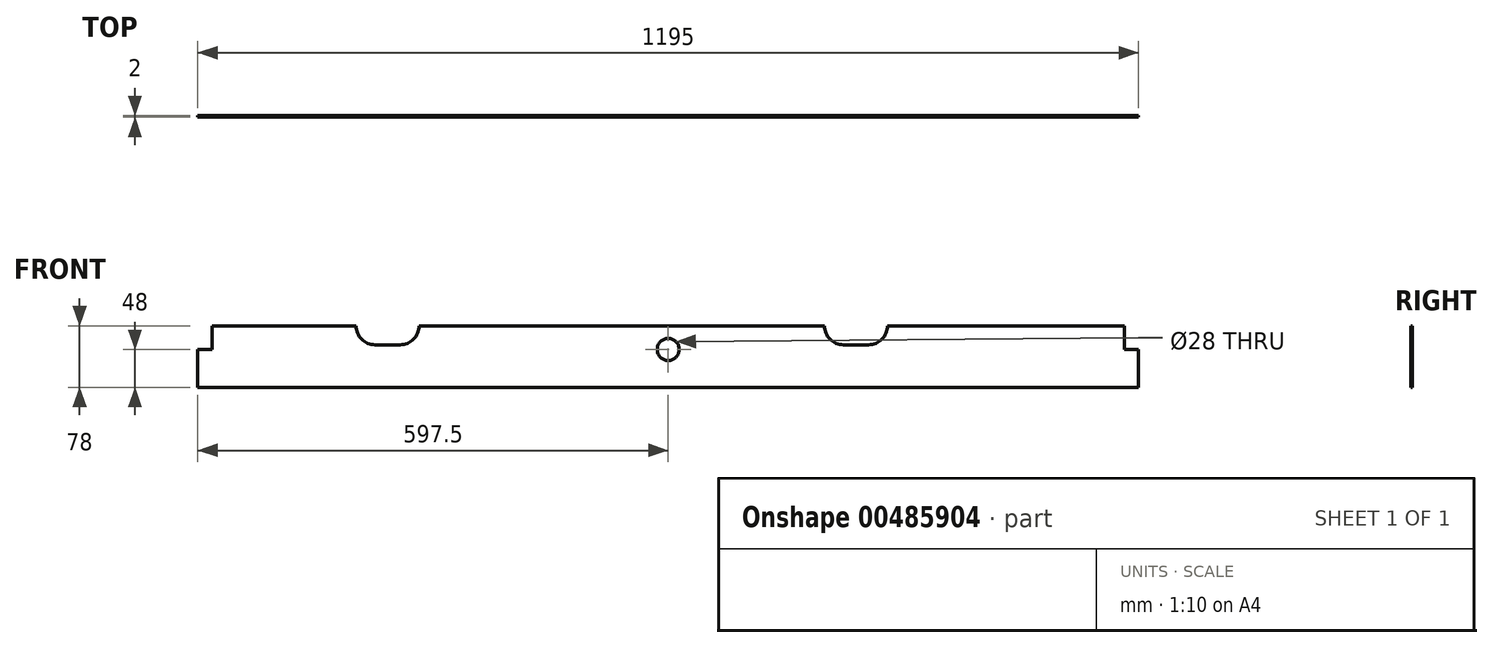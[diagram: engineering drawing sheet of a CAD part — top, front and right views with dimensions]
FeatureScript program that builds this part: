
annotation { "Feature Type Name" : "Feature", "Feature Type Description" : "" }
export const myFeature = defineFeature(function(context is Context, id is Id, definition is map)
    precondition{}
    {
        {
            var Q0;
            Q0=qCreatedBy(makeId("Front.planeOp"),FACE);
            var sketch = newSketch(context, id + "F0", { "sketchPlane" : qUnion([Q0])});
            skLineSegment(sketch, "E0.bottom", {"start": v(597.5, -39) * mm, "end": v(-597.5, -39) * mm});
            skLineSegment(sketch, "E0.top", {"start": v(579.5, 39) * mm, "end": v(278.5, 39) * mm});
            skLineSegment(sketch, "E0.left", {"start": v(597.5, -39) * mm, "end": v(597.5, 9) * mm});
            skLineSegment(sketch, "E0.right", {"start": v(-597.5, -39) * mm, "end": v(-597.5, 9) * mm});
            skPoint(sketch, "E0.middle", {"position": v(0, 0) * mm});
            skLineSegment(sketch, "E1.top", {"start": v(-597.5, 9) * mm, "end": v(-579.5, 9) * mm});
            skLineSegment(sketch, "E1.right", {"start": v(-579.5, 39) * mm, "end": v(-579.5, 9) * mm});
            skPoint(sketch, "E2.orphan", {"position": v(-597.5, 39) * mm});
            skLineSegment(sketch, "E3.top", {"start": v(597.5, 9) * mm, "end": v(579.5, 9) * mm});
            skLineSegment(sketch, "E3.right", {"start": v(579.5, 39) * mm, "end": v(579.5, 9) * mm});
            skPoint(sketch, "E4.orphan", {"position": v(597.5, 39) * mm});
            skLineSegment(sketch, "E5.top", {"start": v(-372.5, 15) * mm, "end": v(-340.5, 15) * mm});
            skLineSegment(sketch, "E5.left", {"start": v(-396.5, 39) * mm, "end": v(-396.5, 39) * mm});
            skPoint(sketch, "E6.visualSharp", {"position": v(-396.5, 15) * mm});
            skArc(sketch, "E6.filletArc", {"start": v(-396.5, 39) * mm, "mid": v(-389.47, 22.03) * mm, "end": v(-372.5, 15) * mm});
            skPoint(sketch, "E7.visualSharp", {"position": v(-316.5, 15) * mm});
            skArc(sketch, "E7.filletArc", {"start": v(-340.5, 15) * mm, "mid": v(-323.53, 22.03) * mm, "end": v(-316.5, 39) * mm});
            skLineSegment(sketch, "E8.trimOffspring", {"start": v(-396.5, 39) * mm, "end": v(-579.5, 39) * mm});
            skLineSegment(sketch, "E9.top", {"start": v(254.5, 15) * mm, "end": v(222.5, 15) * mm});
            skLineSegment(sketch, "E9.left", {"start": v(278.5, 39) * mm, "end": v(278.5, 39) * mm});
            skPoint(sketch, "E10.visualSharp", {"position": v(198.5, 15) * mm});
            skArc(sketch, "E10.filletArc", {"start": v(198.5, 39) * mm, "mid": v(205.53, 22.03) * mm, "end": v(222.5, 15) * mm});
            skPoint(sketch, "E11.visualSharp", {"position": v(278.5, 15) * mm});
            skArc(sketch, "E11.filletArc", {"start": v(254.5, 15) * mm, "mid": v(271.47, 22.03) * mm, "end": v(278.5, 39) * mm});
            skLineSegment(sketch, "E12.trimOffspring", {"start": v(198.5, 39) * mm, "end": v(-316.5, 39) * mm});
            skCircle(sketch, "E13", {"center": v(0, 9) * mm, "radius": 14 * mm});
            skSolve(sketch);
        }
        {
            var Q0;
            Q0=qSketchRegion(id+"F0",true);
            extrude(context, id + "F1", {"entities" : qUnion([Q0]), "depth" : 2 * mm});
        }
    });
